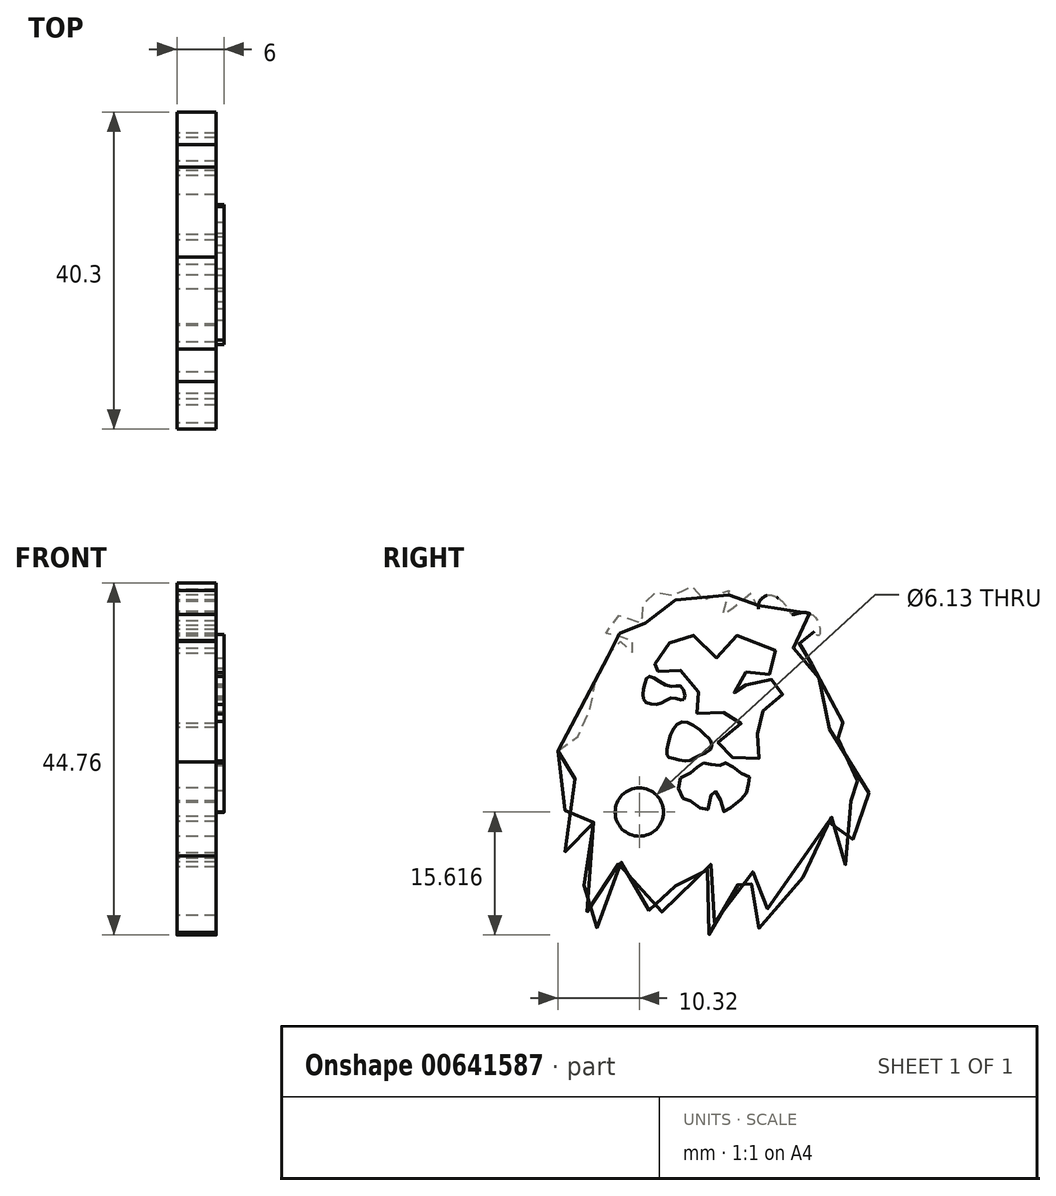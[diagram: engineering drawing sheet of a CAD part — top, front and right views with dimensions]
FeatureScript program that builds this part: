
annotation { "Feature Type Name" : "Feature", "Feature Type Description" : "" }
export const myFeature = defineFeature(function(context is Context, id is Id, definition is map)
    precondition{}
    {
        {
            var Q0;
            Q0=qCreatedBy(makeId("Right.planeOp"),FACE);
            var sketch = newSketch(context, id + "F0", { "sketchPlane" : qUnion([Q0])});
            skFitSpline(sketch, "E0", {"points": [v(-26.25, -4.07) * mm, v(-24.5, -3.12) * mm, v(-22.91, -0.47) * mm, v(-21.85, 2.29) * mm, v(-21.38, 5.15) * mm, v(-19.74, 8.33) * mm, v(-19.36, 9.33) * mm, v(-18.36, 9.8) * mm, v(-17.46, 9.5) * mm, v(-16.82, 8.48) * mm, v(-16.24, 8.38) * mm, v(-16.5, 9.54) * mm, v(-17.83, 10.7) * mm, v(-18.83, 10.7) * mm, v(-19.68, 9.97) * mm, v(-20.1, 10.29) * mm, v(-19.84, 12.14) * mm, v(-18.3, 13.2) * mm, v(-16.34, 12.78) * mm, v(-15.44, 11.88) * mm, v(-15.18, 12.09) * mm, v(-15.55, 12.93) * mm, v(-16.08, 13.84) * mm, v(-15.5, 14.52) * mm, v(-15.04, 15.05) * mm, v(-14.06, 15.96) * mm, v(-13.07, 16.34) * mm, v(-11.97, 15.96) * mm, v(-11.5, 15.22) * mm, v(-11.18, 15.18) * mm, v(-10.38, 16.8) * mm, v(-10.2, 17.29) * mm, v(-8.86, 16.49) * mm, v(-8, 14.95) * mm, v(-7.26, 15.62) * mm, v(-4.45, 16.29) * mm, v(-4.92, 14.95) * mm, v(-5.25, 12.48) * mm, v(-3.85, 14.42) * mm, v(-1.98, 16.35) * mm, v(-1.18, 13.75) * mm, v(-0.85, 13.82) * mm, v(-0.72, 14.82) * mm, v(0, 15.55) * mm, v(0.55, 15.75) * mm, v(1.68, 15.36) * mm, v(2.83, 14.19) * mm, v(3.4, 13.31) * mm, v(3.7, 13.26) * mm, v(4.35, 13.44) * mm, v(5.43, 13.46) * mm, v(6.58, 12.71) * mm, v(6.98, 10.76) * mm, v(6.75, 10.59) * mm, v(6.43, 10.96) * mm, v(5.88, 11.26) * mm, v(5.1, 11.34) * mm, v(4.33, 10.84) * mm, v(3.68, 9.79) * mm, v(3.65, 8.99) * mm, v(4.13, 9.19) * mm, v(4.9, 10.34) * mm, v(5.63, 10.51) * mm, v(6.58, 9.46) * mm, v(6.53, 8.74) * mm, v(6.15, 8.14) * mm, v(6.08, 6.61) * mm, v(6.85, 5.31) * mm, v(8.03, 3.66) * mm, v(9.55, 1.49) * mm, v(9.83, -1.04) * mm, v(9.48, -0.99) * mm, v(8.68, -0.71) * mm, v(8.18, -0.56) * mm, v(7.8, -0.66) * mm, v(8.53, -1.54) * mm, v(9.36, -2.53) * mm, v(10.1, -4) * mm, v(10.67, -5.4) * mm, v(11.05, -6.32) * mm, v(11.4, -6.62) * mm, v(11.6, -7.48) * mm, v(13.1, -9.31) * mm, v(14.04, -10.32) * mm, v(13.6, -10.5) * mm, v(12.73, -10.62) * mm, v(11.2, -10.47) * mm, v(10.82, -10.47) * mm, v(10.86, -11.07) * mm, v(11.27, -12.76) * mm, v(11.12, -15.6) * mm, v(10.07, -18.79) * mm, v(9.85, -17.63) * mm, v(9.85, -15.38) * mm, v(9.29, -13.73) * mm, v(8.5, -12.46) * mm, v(8.24, -12.42) * mm, v(7.97, -15.98) * mm, v(6.89, -18.19) * mm, v(4.5, -20.4) * mm, v(1.93, -22.27) * mm, v(0.6, -23.8) * mm, v(-0.42, -25.5) * mm, v(-1, -27.2) * mm, v(-1.34, -26.9) * mm, v(-2.12, -25.12) * mm, v(-2.04, -22.27) * mm, v(-1.64, -20.87) * mm, v(-1.54, -17.64) * mm, v(-1.77, -17.1) * mm, v(-2.07, -17.1) * mm, v(-2.94, -20.07) * mm, v(-4.64, -22.94) * mm, v(-6, -25.32) * mm, v(-6.5, -26.17) * mm, v(-6.7, -27.37) * mm, v(-7.17, -27.3) * mm, v(-8.1, -24.27) * mm, v(-8.44, -23.2) * mm, v(-8, -20.54) * mm, v(-6.84, -18.47) * mm, v(-6.7, -17.92) * mm, v(-6.74, -17.74) * mm, v(-7.6, -18.37) * mm, v(-10.24, -20.34) * mm, v(-11.97, -21.82) * mm, v(-12.74, -23.02) * mm, v(-13.07, -23.84) * mm, v(-13.17, -24.92) * mm, v(-14.17, -24.42) * mm, v(-14.8, -24.3) * mm, v(-16.5, -23.02) * mm, v(-17.44, -20.67) * mm, v(-17.74, -18.44) * mm, v(-18.12, -18.17) * mm, v(-18.9, -18.77) * mm, v(-20.07, -20.57) * mm, v(-20.84, -23.24) * mm, v(-21.44, -26.92) * mm, v(-21.7, -27.07) * mm, v(-22.2, -25.47) * mm, v(-22.6, -24.3) * mm, v(-22.82, -21.97) * mm, v(-23.04, -20.64) * mm, v(-23.1, -17.54) * mm, v(-22.44, -15.17) * mm, v(-21.84, -13.62) * mm, v(-21.74, -13.12) * mm, v(-22.12, -13.1) * mm, v(-23.22, -14.2) * mm, v(-23.94, -15.12) * mm, v(-25.1, -17.42) * mm, v(-25.34, -16.82) * mm, v(-25.42, -12.74) * mm, v(-25.27, -10.9) * mm, v(-24.38, -8.22) * mm, v(-23.2, -6.47) * mm, v(-22.4, -5.67) * mm, v(-22.77, -5.43) * mm, v(-24.52, -5.34) * mm, v(-26.25, -4.07) * mm]});
            skFitSpline(sketch, "E1", {"points": [v(-12.06, 9.62) * mm, v(-11.35, 10.1) * mm, v(-8.91, 10.57) * mm, v(-6.48, 7.72) * mm, v(-5.46, 8.55) * mm, v(-3.56, 10.57) * mm, v(1.02, 9.09) * mm, v(1.79, 6.11) * mm, v(0, 5.82) * mm, v(-0.89, 6.41) * mm, v(-3.44, 5.22) * mm, v(-3.86, 4.15) * mm, v(-3.68, 2.9) * mm, v(-3.09, 3.26) * mm, v(-2.31, 4.33) * mm, v(0, 4.1) * mm, v(1.25, 5.34) * mm, v(2.09, 3.91) * mm, v(2.15, 2.6) * mm, v(0.54, 1.42) * mm, v(-1.3, 0) * mm, v(-0.89, -1.91) * mm, v(0, -4.3) * mm, v(-1.54, -5.36) * mm, v(-3.32, -5.36) * mm, v(-5.35, -4) * mm, v(-5.7, -3.82) * mm, v(-5.76, -2.39) * mm, v(-3.2, -0.78) * mm, v(-2.97, 0) * mm, v(-4.57, 0.76) * mm, v(-7.19, 0.76) * mm, v(-8.56, 0.7) * mm, v(-8.73, 1) * mm, v(-8.62, 1.95) * mm, v(-8.62, 4.69) * mm, v(-10.52, 6.11) * mm, v(-11.7, 6.35) * mm, v(-13.25, 6.11) * mm, v(-14.8, 6) * mm, v(-14.68, 6.65) * mm, v(-12.48, 7.66) * mm, v(-12.06, 9.62) * mm]});
            skFitSpline(sketch, "E2", {"points": [v(-10.22, 2.49) * mm, v(-10.58, 4.1) * mm, v(-12.18, 4.15) * mm, v(-14.68, 5.4) * mm, v(-15.33, 3.97) * mm, v(-15.28, 2.3) * mm, v(-13.5, 1.9) * mm, v(-11.65, 2.66) * mm, v(-10.22, 2.49) * mm]});
            skFitSpline(sketch, "E3", {"points": [v(-11.59, -5) * mm, v(-12.36, -4.7) * mm, v(-12.18, -2.75) * mm, v(-11.11, -0.67) * mm, v(-9.63, -0.49) * mm, v(-7.43, -2.15) * mm, v(-6.9, -2.69) * mm, v(-6.83, -3.82) * mm, v(-8.56, -4.77) * mm, v(-9.8, -5.36) * mm, v(-11.59, -5) * mm]});
            skFitSpline(sketch, "E4", {"points": [v(-10.7, -7.5) * mm, v(-10.88, -9.17) * mm, v(-10.04, -10.3) * mm, v(-9.03, -10.54) * mm, v(-7.43, -11.78) * mm, v(-6.71, -9.4) * mm, v(-6.36, -9.17) * mm, v(-5.7, -9.94) * mm, v(-5.1, -11.84) * mm, v(-4.1, -11.07) * mm, v(-2.43, -9.7) * mm, v(-2.25, -8.93) * mm, v(-1.84, -7.56) * mm, v(-2.02, -7.32) * mm, v(-3.26, -6.73) * mm, v(-4.4, -5.78) * mm, v(-5.23, -5.6) * mm, v(-5.64, -5.9) * mm, v(-6.83, -5.78) * mm, v(-7.66, -5.6) * mm, v(-8.44, -6.02) * mm, v(-9.1, -6.67) * mm, v(-10.7, -7.5) * mm]});
            skCircle(sketch, "E5", {"center": v(-15.93, -11.84) * mm, "radius": 3.06 * mm});
            skSolve(sketch);
        }
        {
            var Q0;
            Q0 = qSketchRegion(id + "F0", true);
            extrude(context, id + "F1", {"entities" : qUnion([Q0]), "depth" : 5 * mm, "offsetDistance" : 25.4 * mm});
        }
        {
            var Q0;
            Q0=makeQuery(id+"F0.imprint","IMPRINT",FACE,{"disambiguationData":[TD([[makeQuery(id+"F0.imprint","IMPRINT",EDGE,{"derivedFrom":sQuery(id+"F0.wireOp",EDGE,"E2")}),1.0]])]});
            var Q1;
            Q1=makeQuery(id+"F0.imprint","IMPRINT",FACE,{"disambiguationData":[TD([[makeQuery(id+"F0.imprint","IMPRINT",EDGE,{"derivedFrom":sQuery(id+"F0.wireOp",EDGE,"E3")}),-1.0]])]});
            var Q2;
            Q2=makeQuery(id+"F0.imprint","IMPRINT",FACE,{"disambiguationData":[TD([[makeQuery(id+"F0.imprint","IMPRINT",EDGE,{"derivedFrom":sQuery(id+"F0.wireOp",EDGE,"E4")}),1.0]])]});
            var Q3;
            Q3=makeQuery(id+"F0.imprint","IMPRINT",FACE,{"disambiguationData":[TD([[makeQuery(id+"F0.imprint","IMPRINT",EDGE,{"derivedFrom":sQuery(id+"F0.wireOp",EDGE,"E1")}),-1.0]])]});
            extrude(context, id + "F2", {"entities" : qUnion([Q0, Q1, Q2, Q3]), "operationType" : NewBodyOperationType.ADD, "depth" : 6 * mm, "offsetDistance" : 25.4 * mm});
        }
    });
